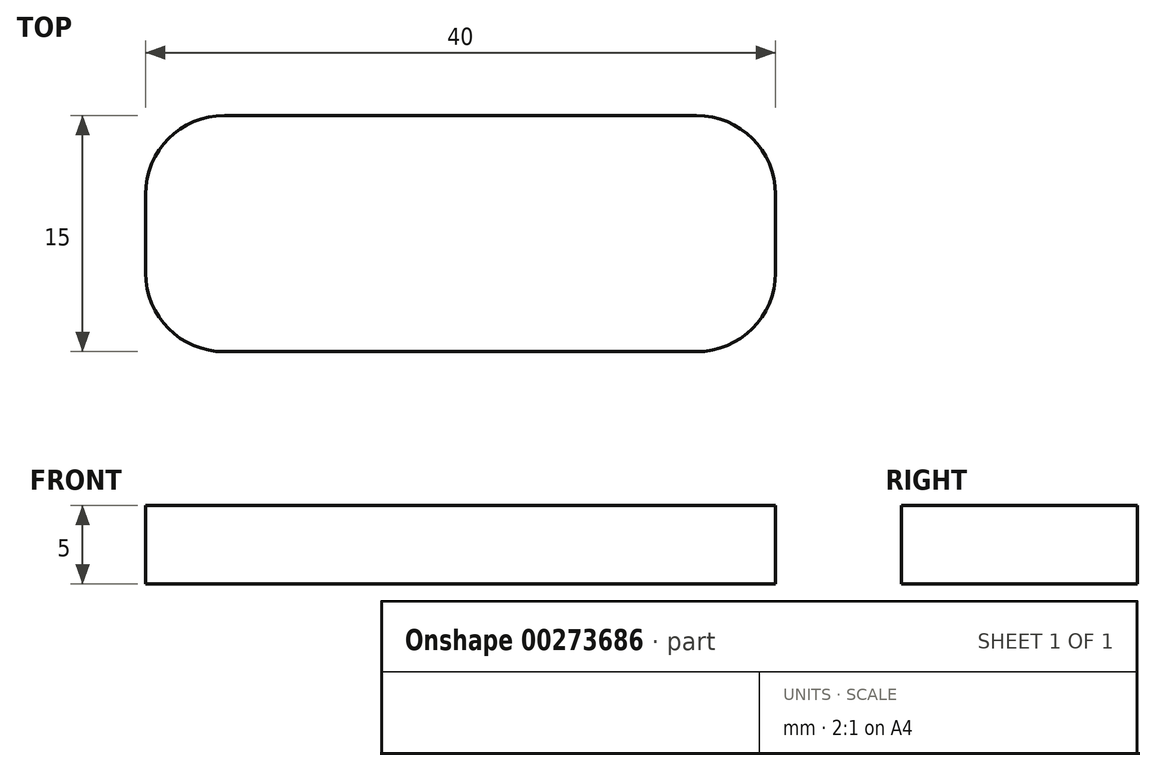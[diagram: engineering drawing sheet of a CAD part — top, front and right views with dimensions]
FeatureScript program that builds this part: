
annotation { "Feature Type Name" : "Feature", "Feature Type Description" : "" }
export const myFeature = defineFeature(function(context is Context, id is Id, definition is map)
    precondition{}
    {
        {
            var Q0;
            Q0=qCreatedBy(makeId("Top.planeOp"),FACE);
            var sketch = newSketch(context, id + "F0", { "sketchPlane" : qUnion([Q0])});
            skLineSegment(sketch, "E0.bottom", {"start": v(0, 0) * mm, "end": v(40, 0) * mm});
            skLineSegment(sketch, "E0.top", {"start": v(0, -15) * mm, "end": v(40, -15) * mm});
            skLineSegment(sketch, "E0.left", {"start": v(0, 0) * mm, "end": v(0, -15) * mm});
            skLineSegment(sketch, "E0.right", {"start": v(40, 0) * mm, "end": v(40, -15) * mm});
            skSolve(sketch);
        }
        {
            var Q0;
            Q0=makeQuery(id+"F0.imprint","IMPRINT",FACE,{"disambiguationData":[TD([[makeQuery(id+"F0.imprint","IMPRINT",EDGE,{"derivedFrom":sQuery(id+"F0.wireOp",EDGE,"E0.bottom")}),-1.0]])]});
            extrude(context, id + "F1", {"entities" : qUnion([Q0]), "depth" : 5 * mm});
        }
        {
            var Q0;
            Q0=makeQuery(id+"F1.opExtrude","SWEPT_EDGE",EDGE,{"disambiguationData":[OSD([sQuery(id+"F0.wireOp",EDGE,"E0.top"),sQuery(id+"F0.wireOp",EDGE,"E0.right")])]});
            var Q1;
            Q1=makeQuery(id+"F1.opExtrude","SWEPT_EDGE",EDGE,{"disambiguationData":[OSD([sQuery(id+"F0.wireOp",EDGE,"E0.bottom"),sQuery(id+"F0.wireOp",EDGE,"E0.right")])]});
            fillet(context, id + "F2", {"entities" : qUnion([Q0, Q1]), "radius" : 5 * mm, "tangentPropagation" : true, "allowEdgeOverflow" : false});
        }
        {
            var Q0;
            Q0=makeQuery(id+"F1.opExtrude","SWEPT_EDGE",EDGE,{"disambiguationData":[OSD([sQuery(id+"F0.wireOp",EDGE,"E0.top"),sQuery(id+"F0.wireOp",EDGE,"E0.left")])]});
            var Q1;
            Q1=makeQuery(id+"F1.opExtrude","SWEPT_EDGE",EDGE,{"disambiguationData":[OSD([sQuery(id+"F0.wireOp",EDGE,"E0.bottom"),sQuery(id+"F0.wireOp",EDGE,"E0.left")])]});
            fillet(context, id + "F3", {"entities" : qUnion([Q0, Q1]), "radius" : 5 * mm, "tangentPropagation" : true, "allowEdgeOverflow" : false});
        }
    });
